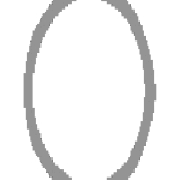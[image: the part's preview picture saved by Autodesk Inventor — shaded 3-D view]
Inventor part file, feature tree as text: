
AUTODESK INVENTOR PART (.ipt)
format: ipt  version: 2021 (Build 250183000, 183)  size: 112,128 bytes
history: native  units: in
note: dims shown in document units (in); Inventor stores cm internally (conversion verified against a paired STEP export)
features: other x4, sketch x3, plane x1
ambient origin geometry x8: Origin, YZ Plane, XZ Plane, XY Plane, X Axis, Y Axis, Z Axis, Center Point
bodies: Solid1 (feature_tree), Body (feature_tree)
feature tree (8):
  other  "Driven Length"
  other  "Frame Generator"
  other  "Start Plane"
  other  "End Plane"
  sketch  "Sketch"  dims[d2=22.0in d4=-0.0in d5=22.0in d6=0.12in d7=0.0in d8=90.0deg d9=22.0in]
  sketch  "Sketch2"  dims[d0=1.0in]
  plane  "Work Plane3"
  sketch  "Sketch3"  dims[d1=0.065in]
